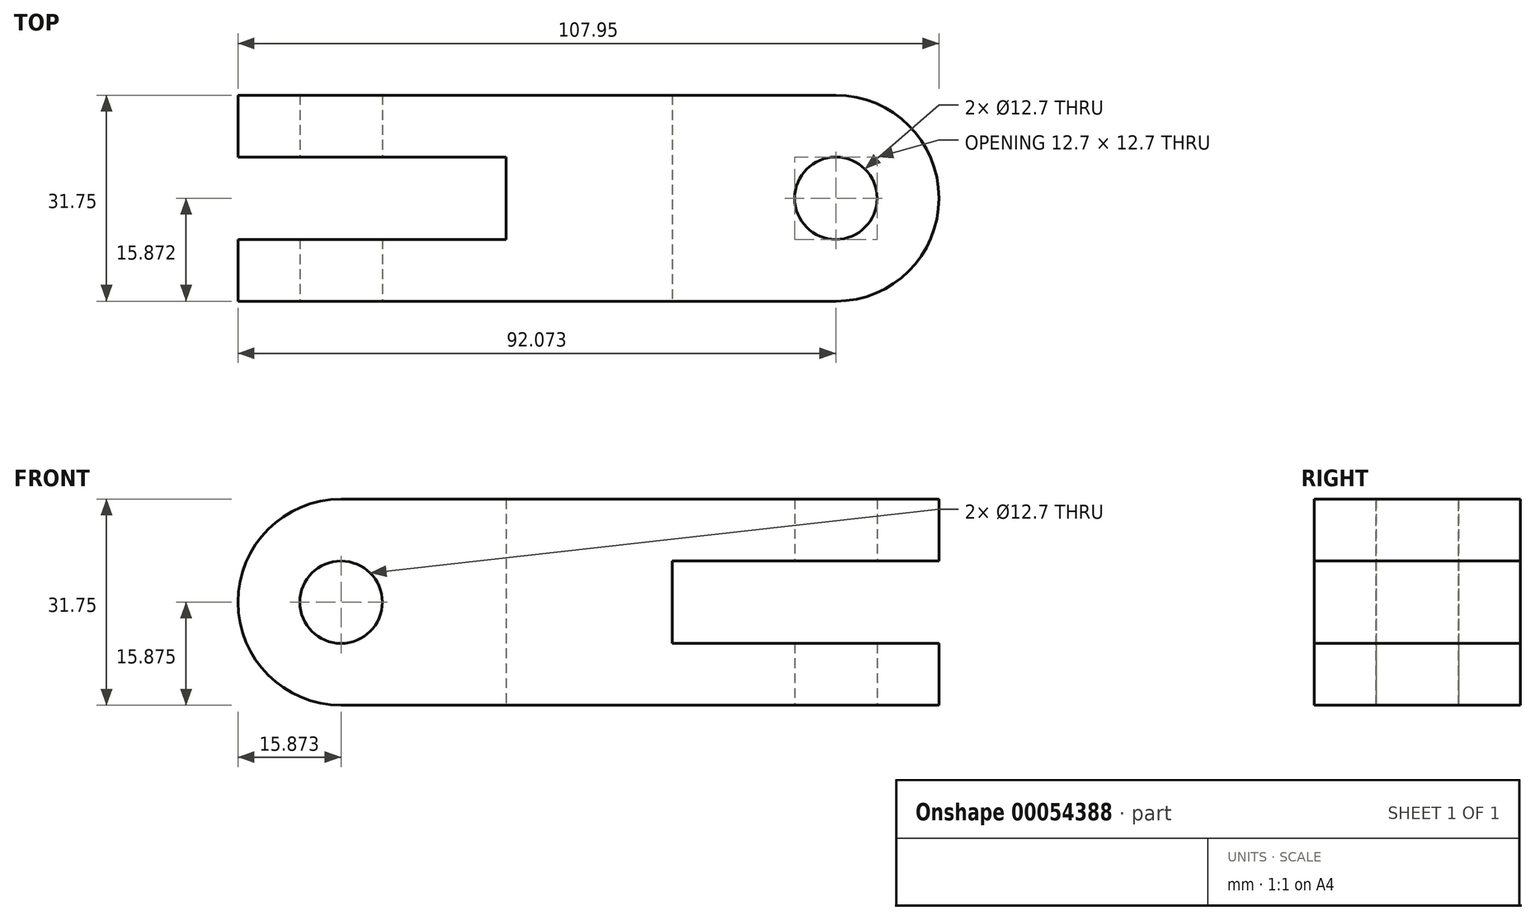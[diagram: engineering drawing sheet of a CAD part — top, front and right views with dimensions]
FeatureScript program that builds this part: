
annotation { "Feature Type Name" : "Feature", "Feature Type Description" : "" }
export const myFeature = defineFeature(function(context is Context, id is Id, definition is map)
    precondition{}
    {
        {
            var Q0;
            Q0=qCreatedBy(makeId("Top.planeOp"),FACE);
            var sketch = newSketch(context, id + "F0", { "sketchPlane" : qUnion([Q0])});
            skLineSegment(sketch, "E0.bottom", {"start": v(-56.5, 13) * mm, "end": v(35.58, 13) * mm});
            skLineSegment(sketch, "E0.top", {"start": v(-56.5, -18.74) * mm, "end": v(35.58, -18.74) * mm});
            skLineSegment(sketch, "E0.left", {"start": v(-56.5, 13) * mm, "end": v(-56.5, -18.74) * mm});
            skLineSegment(sketch, "E1", {"start": v(-56.5, 3.48) * mm, "end": v(21.03, 3.48) * mm});
            skLineSegment(sketch, "E2", {"start": v(-56.5, -9.22) * mm, "end": v(-15.22, -9.22) * mm});
            skLineSegment(sketch, "E3", {"start": v(-15.22, 3.48) * mm, "end": v(-15.22, -9.22) * mm});
            skCircle(sketch, "E4", {"center": v(35.58, -2.87) * mm, "radius": 6.35 * mm});
            skCircle(sketch, "E5", {"center": v(35.58, -2.87) * mm, "radius": 15.88 * mm});
            skLineSegment(sketch, "E6.trimOffspring", {"start": v(50.13, 3.48) * mm, "end": v(51.46, 3.48) * mm});
            skLineSegment(sketch, "E7.trimOffspring", {"start": v(50.13, -9.22) * mm, "end": v(51.46, -9.22) * mm});
            skLineSegment(sketch, "E8", {"start": v(35.58, 13) * mm, "end": v(51.22, 13) * mm});
            skLineSegment(sketch, "E9", {"start": v(51.22, 13) * mm, "end": v(51.46, 3.48) * mm});
            skLineSegment(sketch, "E10", {"start": v(35.58, -18.74) * mm, "end": v(51.64, -18.74) * mm});
            skLineSegment(sketch, "E11", {"start": v(51.46, -9.22) * mm, "end": v(51.64, -18.74) * mm});
            skSolve(sketch);
        }
        {
            var Q0;
            {var subQ6=sQuery(id+"F0.wireOp",EDGE,"E0.top");Q0=makeQuery(id+"F0.imprint","IMPRINT",FACE,{"disambiguationData":[TD([[makeQuery(id+"F0.imprint","IMPRINT",EDGE,{"derivedFrom":subQ6}),1.0]])]});}
            var Q1;
            {var subQ6=sQuery(id+"F0.wireOp",EDGE,"E0.bottom");Q1=makeQuery(id+"F0.imprint","IMPRINT",FACE,{"disambiguationData":[TD([[makeQuery(id+"F0.imprint","IMPRINT",EDGE,{"derivedFrom":subQ6}),-1.0]])]});}
            var Q2;
            Q2=makeQuery(id+"F0.imprint","IMPRINT",FACE,{"disambiguationData":[TD([[makeQuery(id+"F0.imprint","IMPRINT",EDGE,{"derivedFrom":sQuery(id+"F0.wireOp",EDGE,"E4")}),-1.0]])]});
            var Q3;
            {var subQ2=sQuery(id+"F0.wireOp",EDGE,"E7.trimOffspring");Q3=makeQuery(id+"F0.imprint","IMPRINT",FACE,{"disambiguationData":[TD([[makeQuery(id+"F0.imprint","IMPRINT",EDGE,{"derivedFrom":subQ2}),-1.0]])]});}
            var Q4;
            {var subQ2=sQuery(id+"F0.wireOp",EDGE,"E6.trimOffspring");Q4=makeQuery(id+"F0.imprint","IMPRINT",FACE,{"disambiguationData":[TD([[makeQuery(id+"F0.imprint","IMPRINT",EDGE,{"derivedFrom":subQ2}),1.0]])]});}
            extrude(context, id + "F1", {"entities" : qUnion([Q0, Q1, Q2, Q3, Q4]), "depth" : 31.75 * mm});
        }
        {
            var Q0;
            Q0=makeQuery(id+"F1.opExtrude","SWEPT_FACE",FACE,{"disambiguationData":[OSD([sQuery(id+"F0.wireOp",EDGE,"E0.top"),sQuery(id+"F0.wireOp",EDGE,"E10")])]});
            var sketch = newSketch(context, id + "F2", { "sketchPlane" : qUnion([Q0])});
            skLineSegment(sketch, "E12", {"start": v(-56.5, 22.22) * mm, "end": v(51.64, 22.23) * mm});
            skLineSegment(sketch, "E13", {"start": v(-56.5, 9.53) * mm, "end": v(51.64, 9.53) * mm});
            skLineSegment(sketch, "E14", {"start": v(-40.62, 31.75) * mm, "end": v(-40.62, 0) * mm});
            skLineSegment(sketch, "E15", {"start": v(10.36, 31.75) * mm, "end": v(10.36, 0) * mm});
            skCircle(sketch, "E16", {"center": v(-40.62, 15.88) * mm, "radius": 6.35 * mm});
            skCircle(sketch, "E17", {"center": v(-40.62, 15.88) * mm, "radius": 15.88 * mm});
            skSolve(sketch);
        }
        {
            var Q0;
            Q0 = qSketchRegion(id + "F0", true);
            extrude(context, id + "F3", {"entities" : qUnion([Q0]), "operationType" : NewBodyOperationType.REMOVE, "oppositeDirection" : true, "depth" : 31.75 * mm});
        }
        {
            var Q0;
            {var subQ0=sQuery(id+"F2.wireOp",EDGE,"E12");var subQ4=sQuery(id+"F2.wireOp",EDGE,"E17");var subQ5=makeQuery(id+"F2.imprint","INTERSECT",VERTEX,{"disambiguationData":[OD(0.0)],"derivedFrom":[subQ0,subQ4]});Q0=makeQuery(id+"F2.imprint","IMPRINT",FACE,{"disambiguationData":[TD([[makeQuery(id+"F2.imprint","IMPRINT",EDGE,{"disambiguationData":[TD([[subQ5,1.0]])],"derivedFrom":subQ0}),1.0]])]});}
            var Q1;
            {var subQ0=sQuery(id+"F2.wireOp",EDGE,"E12");var subQ3=sQuery(id+"F2.wireOp",EDGE,"E17");var subQ4=makeQuery(id+"F2.imprint","INTERSECT",VERTEX,{"disambiguationData":[OD(0.0)],"derivedFrom":[subQ0,subQ3]});Q1=makeQuery(id+"F2.imprint","IMPRINT",FACE,{"disambiguationData":[TD([[makeQuery(id+"F2.imprint","IMPRINT",EDGE,{"disambiguationData":[TD([[subQ4,1.0]])],"derivedFrom":subQ0}),-1.0]])]});}
            var Q2;
            {var subQ0=sQuery(id+"F2.wireOp",EDGE,"E13");var subQ3=sQuery(id+"F2.wireOp",EDGE,"E17");var subQ4=makeQuery(id+"F2.imprint","INTERSECT",VERTEX,{"disambiguationData":[OD(0.0)],"derivedFrom":[subQ0,subQ3]});Q2=makeQuery(id+"F2.imprint","IMPRINT",FACE,{"disambiguationData":[TD([[makeQuery(id+"F2.imprint","IMPRINT",EDGE,{"disambiguationData":[TD([[subQ4,1.0]])],"derivedFrom":subQ0}),1.0]])]});}
            var Q3;
            {var subQ0=sQuery(id+"F2.wireOp",EDGE,"E13");var subQ4=sQuery(id+"F2.wireOp",EDGE,"E17");var subQ5=makeQuery(id+"F2.imprint","INTERSECT",VERTEX,{"disambiguationData":[OD(0.0)],"derivedFrom":[subQ0,subQ4]});Q3=makeQuery(id+"F2.imprint","IMPRINT",FACE,{"disambiguationData":[TD([[makeQuery(id+"F2.imprint","IMPRINT",EDGE,{"disambiguationData":[TD([[subQ5,1.0]])],"derivedFrom":subQ0}),-1.0]])]});}
            var Q4;
            {var subQ0=sQuery(id+"F2.wireOp",EDGE,"E16");var subQ1=sQuery(id+"F2.wireOp",EDGE,"E14");var subQ2=makeQuery(id+"F2.imprint","INTERSECT",VERTEX,{"derivedFrom":[sQuery(id+"F2.wireOp",EDGE,"E12"),subQ1,subQ0]});Q4=makeQuery(id+"F2.imprint","IMPRINT",FACE,{"disambiguationData":[TD([[makeQuery(id+"F2.imprint","IMPRINT",EDGE,{"disambiguationData":[TD([[subQ2,-1.0]])],"derivedFrom":subQ1}),-1.0]])]});}
            var Q5;
            {var subQ0=sQuery(id+"F2.wireOp",EDGE,"E16");var subQ1=sQuery(id+"F2.wireOp",EDGE,"E14");var subQ2=makeQuery(id+"F2.imprint","INTERSECT",VERTEX,{"derivedFrom":[sQuery(id+"F2.wireOp",EDGE,"E12"),subQ1,subQ0]});Q5=makeQuery(id+"F2.imprint","IMPRINT",FACE,{"disambiguationData":[TD([[makeQuery(id+"F2.imprint","IMPRINT",EDGE,{"disambiguationData":[TD([[subQ2,-1.0]])],"derivedFrom":subQ1}),1.0]])]});}
            var Q6;
            {var subQ0=sQuery(id+"F2.wireOp",EDGE,"E12");var subQ3=sQuery(id+"F2.wireOp",EDGE,"E15");var subQ4=makeQuery(id+"F2.imprint","INTERSECT",VERTEX,{"derivedFrom":[subQ0,subQ3]});Q6=makeQuery(id+"F2.imprint","IMPRINT",FACE,{"disambiguationData":[TD([[makeQuery(id+"F2.imprint","IMPRINT",EDGE,{"disambiguationData":[TD([[subQ4,-1.0]])],"derivedFrom":subQ3}),1.0]])]});}
            extrude(context, id + "F4", {"entities" : qUnion([Q0, Q1, Q2, Q3, Q4, Q5, Q6]), "operationType" : NewBodyOperationType.REMOVE, "endBound" : BoundingType.THROUGH_ALL, "oppositeDirection" : true, "depth" : 25.4 * mm});
        }
        {
            var Q0;
            {var subQ2=sQuery(id+"F0.wireOp",EDGE,"E6.trimOffspring");Q0=makeQuery(id+"F0.imprint","IMPRINT",FACE,{"disambiguationData":[TD([[makeQuery(id+"F0.imprint","IMPRINT",EDGE,{"derivedFrom":subQ2}),1.0]])]});}
            var Q1;
            {var subQ2=sQuery(id+"F0.wireOp",EDGE,"E7.trimOffspring");Q1=makeQuery(id+"F0.imprint","IMPRINT",FACE,{"disambiguationData":[TD([[makeQuery(id+"F0.imprint","IMPRINT",EDGE,{"derivedFrom":subQ2}),-1.0]])]});}
            extrude(context, id + "F5", {"entities" : qUnion([Q0, Q1]), "operationType" : NewBodyOperationType.REMOVE, "endBound" : BoundingType.THROUGH_ALL, "depth" : 25.4 * mm});
        }
    });
